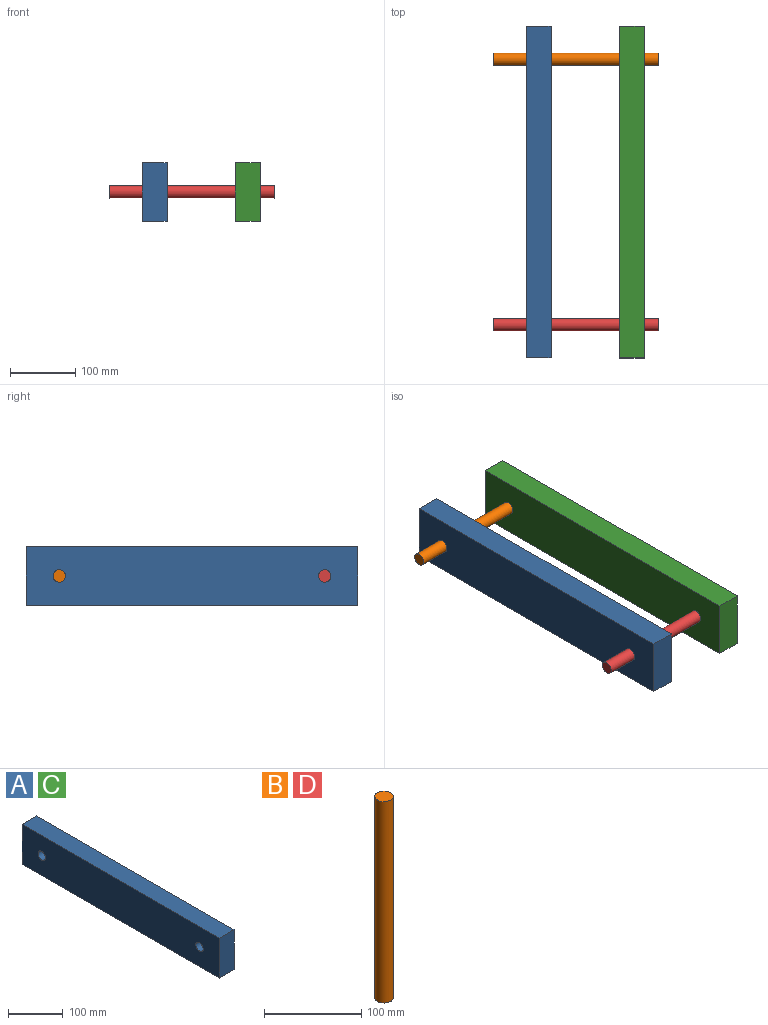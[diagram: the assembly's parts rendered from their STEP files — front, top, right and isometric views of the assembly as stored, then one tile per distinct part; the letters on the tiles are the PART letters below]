
ASSEMBLY  parts=4 mates=3
PART A: 8 faces, bbox 38.1x508x88.9 mm
  f0: plane 508x38.1mm, normal (0,0,1), area 19354.8mm2, adj f1,f3,f4,f5
  f1: plane 508x88.9mm, normal (-1,0,0), area 44591.2mm2, adj f0,f2,f4,f5,f6,f7
  f2: plane 508x38.1mm, normal (0,0,-1), area 19354.8mm2, adj f1,f3,f4,f5
  f3: plane 508x88.9mm, normal (1,0,0), area 44591.2mm2, adj f0,f2,f4,f5,f6,f7
  f4: plane 88.9x38.1mm, normal (0,-1,0), area 3387.1mm2, adj f0,f1,f2,f3
  f5: plane 88.9x38.1mm, normal (0,1,0), area 3387.1mm2, adj f0,f1,f2,f3
  f6: cylinder r=9.53mm len=38.1mm, axis (-1,0,0), area 2280.2mm2, adj f1,f3
  f7: cylinder r=9.53mm len=38.1mm, axis (-1,0,0), area 2280.2mm2, adj f1,f3
PART B: 3 faces, bbox 19.1x19.1x254 mm
  f0: cylinder r=9.53mm len=254mm, axis (0,0,-1), area 15201.2mm2, adj f1,f2
  f1: plane 19.05x19.05mm, normal (0,0,1), area 285mm2, adj f0
  f2: plane 19.05x19.05mm, normal (0,0,-1), area 285mm2, adj f0
PART C: same geometry as A
PART D: same geometry as B
PLACE A t=(-327.65,-55.17,62.17)mm
PLACE B rot(axis=(0,-1,0),90deg) t=(-183.11,-142.93,135.57)mm
PLACE C t=(-184.91,-55.17,62.17)mm
PLACE D rot(axis=(0,-1,0),90deg) t=(-183.11,-549.33,135.57)mm
MATE slider D.f0 <-> C.f7  axis (1,0,0) through (-183.11,-512.37,102.64)mm
MATE fastened D.f0 <-> A.f7  axis (-1,0,0) through (-437.11,-512.37,102.64)mm
MATE fastened B.f0 <-> A.f6  axis (-1,0,0) through (-437.11,-105.97,102.64)mm
